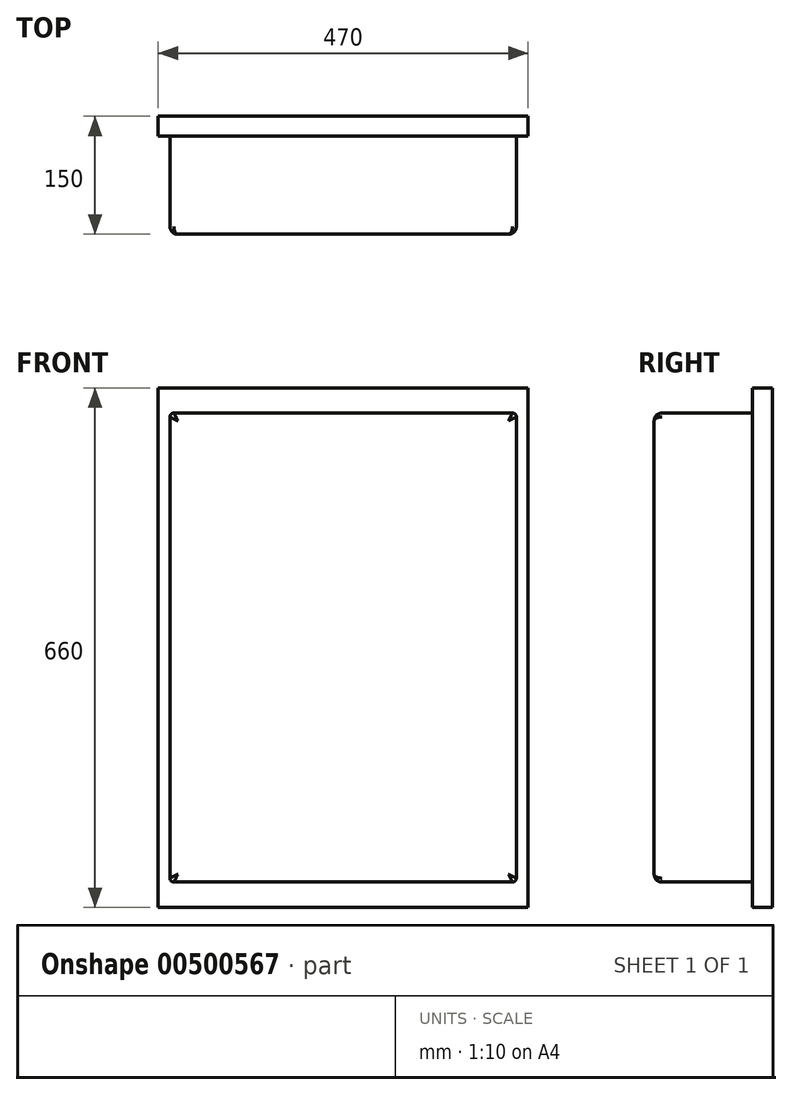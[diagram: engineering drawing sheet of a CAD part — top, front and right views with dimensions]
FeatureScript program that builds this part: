
annotation { "Feature Type Name" : "Feature", "Feature Type Description" : "" }
export const myFeature = defineFeature(function(context is Context, id is Id, definition is map)
    precondition{}
    {
        {
            var Q0;
            Q0=qCreatedBy(makeId("Front.planeOp"),FACE);
            var sketch = newSketch(context, id + "F0", { "sketchPlane" : qUnion([Q0])});
            skLineSegment(sketch, "E0.bottom", {"start": v(235, 330) * mm, "end": v(-235, 330) * mm});
            skLineSegment(sketch, "E0.top", {"start": v(235, -330) * mm, "end": v(-235, -330) * mm});
            skLineSegment(sketch, "E0.left", {"start": v(235, 330) * mm, "end": v(235, -330) * mm});
            skLineSegment(sketch, "E0.right", {"start": v(-235, 330) * mm, "end": v(-235, -330) * mm});
            skPoint(sketch, "E0.middle", {"position": v(0, 0) * mm});
            skLineSegment(sketch, "E1.bottom", {"start": v(220, 298) * mm, "end": v(-220, 298) * mm});
            skLineSegment(sketch, "E1.top", {"start": v(220, -298) * mm, "end": v(-220, -298) * mm});
            skLineSegment(sketch, "E1.left", {"start": v(220, 298) * mm, "end": v(220, -298) * mm});
            skLineSegment(sketch, "E1.right", {"start": v(-220, 298) * mm, "end": v(-220, -298) * mm});
            skSolve(sketch);
        }
        {
            var Q0;
            Q0=makeQuery(id+"F0.imprint","IMPRINT",FACE,{"disambiguationData":[TD([[makeQuery(id+"F0.imprint","IMPRINT",EDGE,{"derivedFrom":sQuery(id+"F0.wireOp",EDGE,"E0.bottom")}),1.0]])]});
            extrude(context, id + "F1", {"entities" : qUnion([Q0]), "depth" : 25 * mm});
        }
        {
            var Q0;
            Q0=makeQuery(id+"F0.imprint","IMPRINT",FACE,{"disambiguationData":[TD([[makeQuery(id+"F0.imprint","IMPRINT",EDGE,{"derivedFrom":sQuery(id+"F0.wireOp",EDGE,"E1.bottom")}),1.0]])]});
            extrude(context, id + "F2", {"entities" : qUnion([Q0]), "operationType" : NewBodyOperationType.ADD, "depth" : 150 * mm});
        }
        {
            var Q0;
            Q0=makeQuery(id+"F2.opExtrude","CAP_FACE",FACE,{"disambiguationData":[OSD([sQuery(id+"F0.wireOp",EDGE,"E1.bottom"),sQuery(id+"F0.wireOp",EDGE,"E1.top"),sQuery(id+"F0.wireOp",EDGE,"E1.left"),sQuery(id+"F0.wireOp",EDGE,"E1.right")])],"isStart":false});
            fillet(context, id + "F3", {"entities" : qUnion([Q0]), "radius" : 10 * mm, "tangentPropagation" : true, "allowEdgeOverflow" : false});
        }
        {
            var Q0;
            Q0=makeQuery(id+"F2.opExtrude","SWEPT_EDGE",EDGE,{"disambiguationData":[OSD([sQuery(id+"F0.wireOp",EDGE,"E1.bottom"),sQuery(id+"F0.wireOp",EDGE,"E1.left")])]});
            var Q1;
            Q1=makeQuery(id+"F2.opExtrude","SWEPT_EDGE",EDGE,{"disambiguationData":[OSD([sQuery(id+"F0.wireOp",EDGE,"E1.bottom"),sQuery(id+"F0.wireOp",EDGE,"E1.right")])]});
            var Q2;
            Q2=makeQuery(id+"F2.opExtrude","SWEPT_EDGE",EDGE,{"disambiguationData":[OSD([sQuery(id+"F0.wireOp",EDGE,"E1.top"),sQuery(id+"F0.wireOp",EDGE,"E1.left")])]});
            var Q3;
            Q3=makeQuery(id+"F2.opExtrude","SWEPT_EDGE",EDGE,{"disambiguationData":[OSD([sQuery(id+"F0.wireOp",EDGE,"E1.top"),sQuery(id+"F0.wireOp",EDGE,"E1.right")])]});
            fillet(context, id + "F4", {"entities" : qUnion([Q0, Q1, Q2, Q3]), "radius" : 5 * mm, "tangentPropagation" : true, "allowEdgeOverflow" : false});
        }
    });
